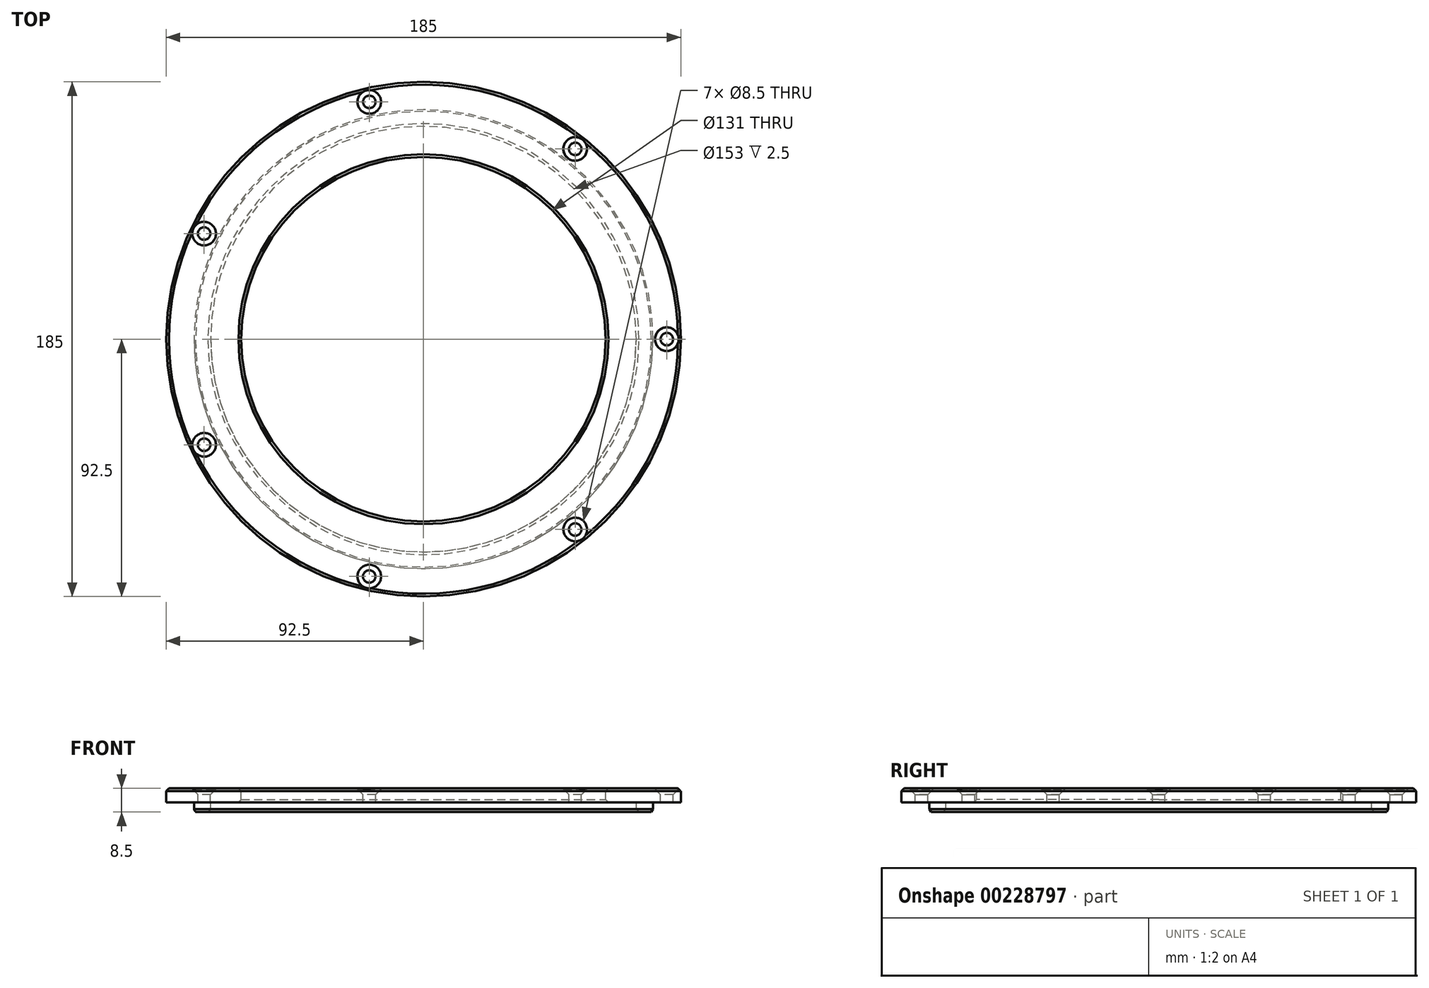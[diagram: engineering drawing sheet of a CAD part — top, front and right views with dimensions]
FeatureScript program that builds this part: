
annotation { "Feature Type Name" : "Feature", "Feature Type Description" : "" }
export const myFeature = defineFeature(function(context is Context, id is Id, definition is map)
    precondition{}
    {
        {
            var Q0;
            Q0=qCreatedBy(makeId("Right.planeOp"),FACE);
            var sketch = newSketch(context, id + "F0", { "sketchPlane" : qUnion([Q0])});
            skLineSegment(sketch, "E0", {"start": v(92.5, 0) * mm, "end": v(82.5, 0) * mm});
            skLineSegment(sketch, "E1", {"start": v(82.5, 0) * mm, "end": v(82.5, -3.5) * mm});
            skLineSegment(sketch, "E2", {"start": v(82.5, -3.5) * mm, "end": v(76.5, -3.5) * mm});
            skLineSegment(sketch, "E3", {"start": v(76.5, -3.5) * mm, "end": v(76.5, 0) * mm});
            skLineSegment(sketch, "E4", {"start": v(76.5, 0) * mm, "end": v(65.5, 0) * mm});
            skLineSegment(sketch, "E5", {"start": v(65.5, 0) * mm, "end": v(65.5, 5) * mm});
            skLineSegment(sketch, "E6", {"start": v(65.5, 5) * mm, "end": v(92.5, 5) * mm});
            skLineSegment(sketch, "E7", {"start": v(92.5, 5) * mm, "end": v(92.5, 0) * mm});
            skLineSegment(sketch, "E8", {"start": v(0, 32.72) * mm, "end": v(0, -33.1) * mm, "construction": true});
            skSolve(sketch);
        }
        {
            var Q0;
            Q0 = qSketchRegion(id + "F0", true);
            var Q1;
            Q1=sQuery(id+"F0.wireOp",EDGE,"E8");
            revolve(context, id + "F1", {"entities" : qUnion([Q0]), "axis" : qUnion([Q1]), "revolveType" : RevolveType.FULL});
        }
        {
            var Q0;
            Q0=makeQuery(id+"F1.opRevolve","SWEPT_EDGE",EDGE,{"disambiguationData":[OSD([sQuery(id+"F0.wireOp",EDGE,"E6"),sQuery(id+"F0.wireOp",EDGE,"E7")])]});
            var Q1;
            Q1=makeQuery(id+"F1.opRevolve","SWEPT_EDGE",EDGE,{"disambiguationData":[OSD([sQuery(id+"F0.wireOp",EDGE,"E5"),sQuery(id+"F0.wireOp",EDGE,"E6")])]});
            var Q2;
            Q2=makeQuery(id+"F1.opRevolve","SWEPT_EDGE",EDGE,{"disambiguationData":[OSD([sQuery(id+"F0.wireOp",EDGE,"E4"),sQuery(id+"F0.wireOp",EDGE,"E5")])]});
            var Q3;
            Q3=makeQuery(id+"F1.opRevolve","SWEPT_EDGE",EDGE,{"disambiguationData":[OSD([sQuery(id+"F0.wireOp",EDGE,"E2"),sQuery(id+"F0.wireOp",EDGE,"E3")])]});
            chamfer(context, id + "F2", {"entities" : qUnion([Q0, Q1, Q2, Q3]), "width" : 1 * mm, "tangentPropagation" : true});
        }
        {
            var Q0;
            Q0=makeQuery(id+"F1.opRevolve","SWEPT_FACE",FACE,{"disambiguationData":[OSD([sQuery(id+"F0.wireOp",EDGE,"E6")])]});
            var sketch = newSketch(context, id + "F3", { "sketchPlane" : qUnion([Q0])});
            skCircle(sketch, "E9", {"center": v(0, 0) * mm, "radius": 87.5 * mm, "construction": true});
            skLineSegment(sketch, "E10", {"start": v(0, 0) * mm, "end": v(87.5, 0) * mm, "construction": true});
            skPoint(sketch, "E11", {"position": v(87.5, 0) * mm});
            skPoint(sketch, "E12.1.0", {"position": v(54.56, 68.41) * mm});
            skPoint(sketch, "E12.2.0", {"position": v(-19.47, 85.3) * mm});
            skPoint(sketch, "E12.3.0", {"position": v(-78.83, 37.96) * mm});
            skPoint(sketch, "E12.4.0", {"position": v(-78.83, -37.96) * mm});
            skPoint(sketch, "E12.5.0", {"position": v(-19.47, -85.3) * mm});
            skPoint(sketch, "E12.6.0", {"position": v(54.56, -68.41) * mm});
            skSolve(sketch);
        }
        {
            var Q0;
            Q0=sQuery(id+"F3.wireOp",VERTEX,"E11");
            var Q1;
            Q1=sQuery(id+"F3.wireOp",VERTEX,"E12.1.0");
            var Q2;
            Q2=sQuery(id+"F3.wireOp",VERTEX,"E12.2.0");
            var Q3;
            Q3=sQuery(id+"F3.wireOp",VERTEX,"E12.3.0");
            var Q4;
            Q4=sQuery(id+"F3.wireOp",VERTEX,"E12.4.0");
            var Q5;
            Q5=sQuery(id+"F3.wireOp",VERTEX,"E12.5.0");
            var Q6;
            Q6=sQuery(id+"F3.wireOp",VERTEX,"E12.6.0");
            var Q7;
            Q7=makeQuery(id+"F1.opRevolve","SWEPT_BODY",BODY,{"disambiguationData":[OSD([sQuery(id+"F0.wireOp",EDGE,"E0"),sQuery(id+"F0.wireOp",EDGE,"E1"),sQuery(id+"F0.wireOp",EDGE,"E2"),sQuery(id+"F0.wireOp",EDGE,"E3"),sQuery(id+"F0.wireOp",EDGE,"E4"),sQuery(id+"F0.wireOp",EDGE,"E5"),sQuery(id+"F0.wireOp",EDGE,"E6"),sQuery(id+"F0.wireOp",EDGE,"E7")])]});
            hole(context, id + "F4", {"style" : HoleStyle.C_SINK, "endStyle" : HoleEndStyle.THROUGH, "holeDiameter" : 4.5 * mm, "cSinkDiameter" : 8.5 * mm, "cSinkAngle" : 90 * degree, "locations" : qUnion([Q0, Q1, Q2, Q3, Q4, Q5, Q6]), "scope" : qUnion([Q7]), "isTappedThrough" : true});
        }
        {
            var Q0;
            Q0=makeQuery(id+"F1.opRevolve","SWEPT_EDGE",EDGE,{"disambiguationData":[OSD([sQuery(id+"F0.wireOp",EDGE,"E1"),sQuery(id+"F0.wireOp",EDGE,"E2")])]});
            chamfer(context, id + "F5", {"entities" : qUnion([Q0]), "chamferType" : ChamferType.OFFSET_ANGLE, "width" : 1 * mm, "oppositeDirection" : false, "angle" : 30 * degree, "tangentPropagation" : true});
        }
    });
